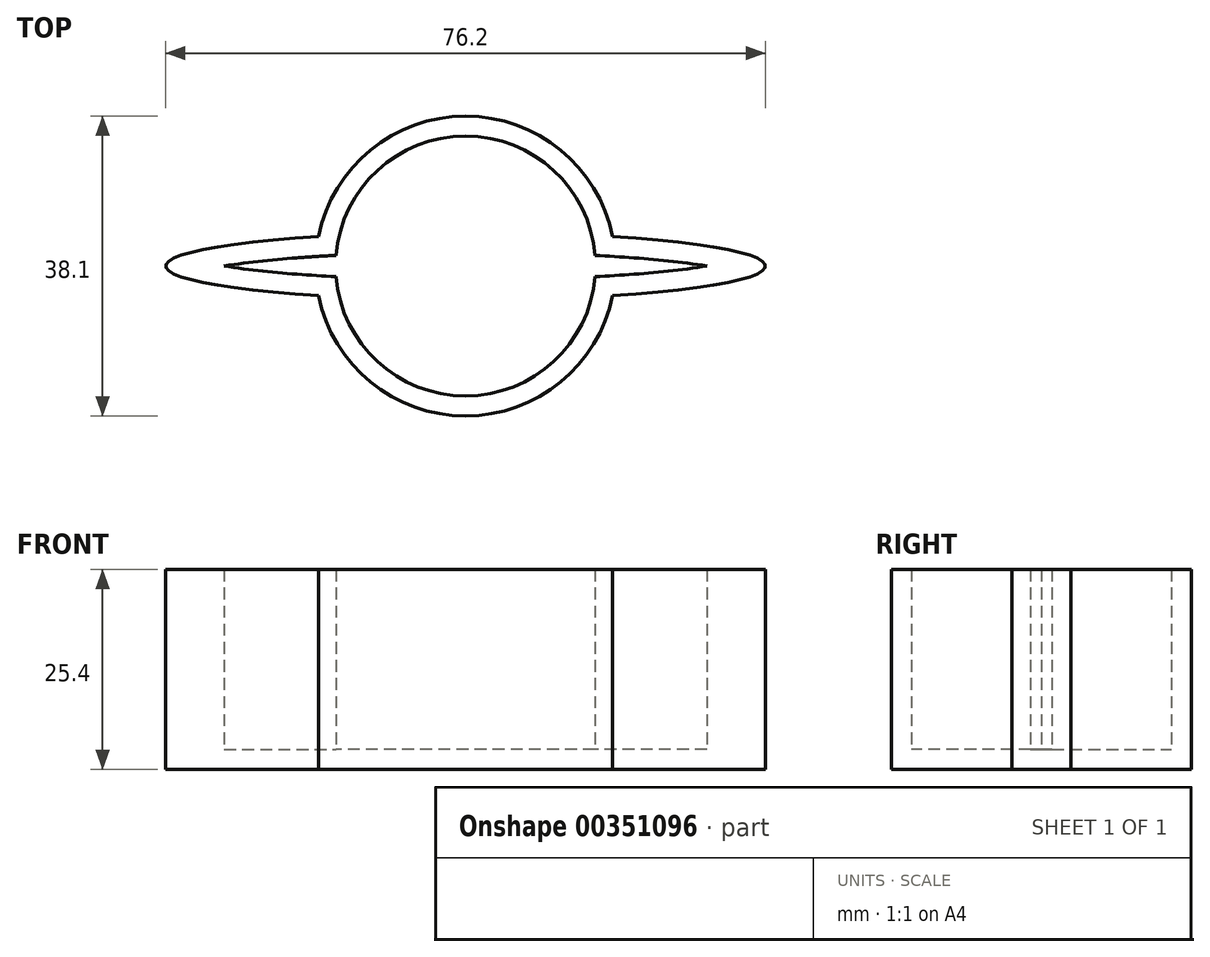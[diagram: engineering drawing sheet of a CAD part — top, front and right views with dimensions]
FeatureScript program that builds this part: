
annotation { "Feature Type Name" : "Feature", "Feature Type Description" : "" }
export const myFeature = defineFeature(function(context is Context, id is Id, definition is map)
    precondition{}
    {
        {
            var Q0;
            Q0=qCreatedBy(makeId("Top.planeOp"),FACE);
            var sketch = newSketch(context, id + "F0", { "sketchPlane" : qUnion([Q0])});
            skCircle(sketch, "E0", {"center": v(0, 0) * mm, "radius": 19.05 * mm});
            skEllipse(sketch, "E1", {"center": v(0, 0) * mm, "majorRadius": 38.1 * mm, "minorRadius": 4.33 * mm, "majorAxis": v(1, 0)});
            skSolve(sketch);
        }
        {
            var Q0;
            {var subQ0=sQuery(id+"F0.wireOp",EDGE,"E1");var subQ1=sQuery(id+"F0.wireOp",EDGE,"E0");var subQ2=makeQuery(id+"F0.imprint","INTERSECT",VERTEX,{"disambiguationData":[OD(0.0)],"derivedFrom":[subQ1,subQ0]});Q0=makeQuery(id+"F0.imprint","IMPRINT",FACE,{"disambiguationData":[TD([[makeQuery(id+"F0.imprint","IMPRINT",EDGE,{"disambiguationData":[TD([[subQ2,-1.0]])],"derivedFrom":subQ1}),1.0]])]});}
            var Q1;
            {var subQ0=sQuery(id+"F0.wireOp",EDGE,"E1");var subQ1=sQuery(id+"F0.wireOp",EDGE,"E0");var subQ2=makeQuery(id+"F0.imprint","INTERSECT",VERTEX,{"disambiguationData":[OD(1.0)],"derivedFrom":[subQ1,subQ0]});Q1=makeQuery(id+"F0.imprint","IMPRINT",FACE,{"disambiguationData":[TD([[makeQuery(id+"F0.imprint","IMPRINT",EDGE,{"disambiguationData":[TD([[subQ2,1.0]])],"derivedFrom":subQ1}),-1.0]])]});}
            var Q2;
            {var subQ0=sQuery(id+"F0.wireOp",EDGE,"E1");var subQ1=sQuery(id+"F0.wireOp",EDGE,"E0");var subQ2=makeQuery(id+"F0.imprint","INTERSECT",VERTEX,{"disambiguationData":[OD(2.0)],"derivedFrom":[subQ1,subQ0]});Q2=makeQuery(id+"F0.imprint","IMPRINT",FACE,{"disambiguationData":[TD([[makeQuery(id+"F0.imprint","IMPRINT",EDGE,{"disambiguationData":[TD([[subQ2,-1.0]])],"derivedFrom":subQ1}),1.0]])]});}
            var Q3;
            {var subQ0=sQuery(id+"F0.wireOp",EDGE,"E1");var subQ1=sQuery(id+"F0.wireOp",EDGE,"E0");var subQ2=makeQuery(id+"F0.imprint","INTERSECT",VERTEX,{"disambiguationData":[OD(0.0)],"derivedFrom":[subQ1,subQ0]});Q3=makeQuery(id+"F0.imprint","IMPRINT",FACE,{"disambiguationData":[TD([[makeQuery(id+"F0.imprint","IMPRINT",EDGE,{"disambiguationData":[TD([[subQ2,-1.0]])],"derivedFrom":subQ1}),-1.0]])]});}
            var Q4;
            {var subQ0=sQuery(id+"F0.wireOp",EDGE,"E1");var subQ1=sQuery(id+"F0.wireOp",EDGE,"E0");var subQ2=makeQuery(id+"F0.imprint","INTERSECT",VERTEX,{"disambiguationData":[OD(0.0)],"derivedFrom":[subQ1,subQ0]});Q4=makeQuery(id+"F0.imprint","IMPRINT",FACE,{"disambiguationData":[TD([[makeQuery(id+"F0.imprint","IMPRINT",EDGE,{"disambiguationData":[TD([[subQ2,1.0]])],"derivedFrom":subQ1}),1.0]])]});}
            extrude(context, id + "F1", {"entities" : qUnion([Q0, Q1, Q2, Q3, Q4]), "depth" : 25.4 * mm});
        }
        {
            var Q0;
            Q0=makeQuery(id+"F1.opExtrude","CAP_FACE",FACE,{"disambiguationData":[OSD([sQuery(id+"F0.wireOp",EDGE,"E0"),sQuery(id+"F0.wireOp",EDGE,"E1")])],"isStart":false});
            shell(context, id + "F2", {"entities" : qUnion([Q0]), "thickness" : 2.54 * mm});
        }
    });
